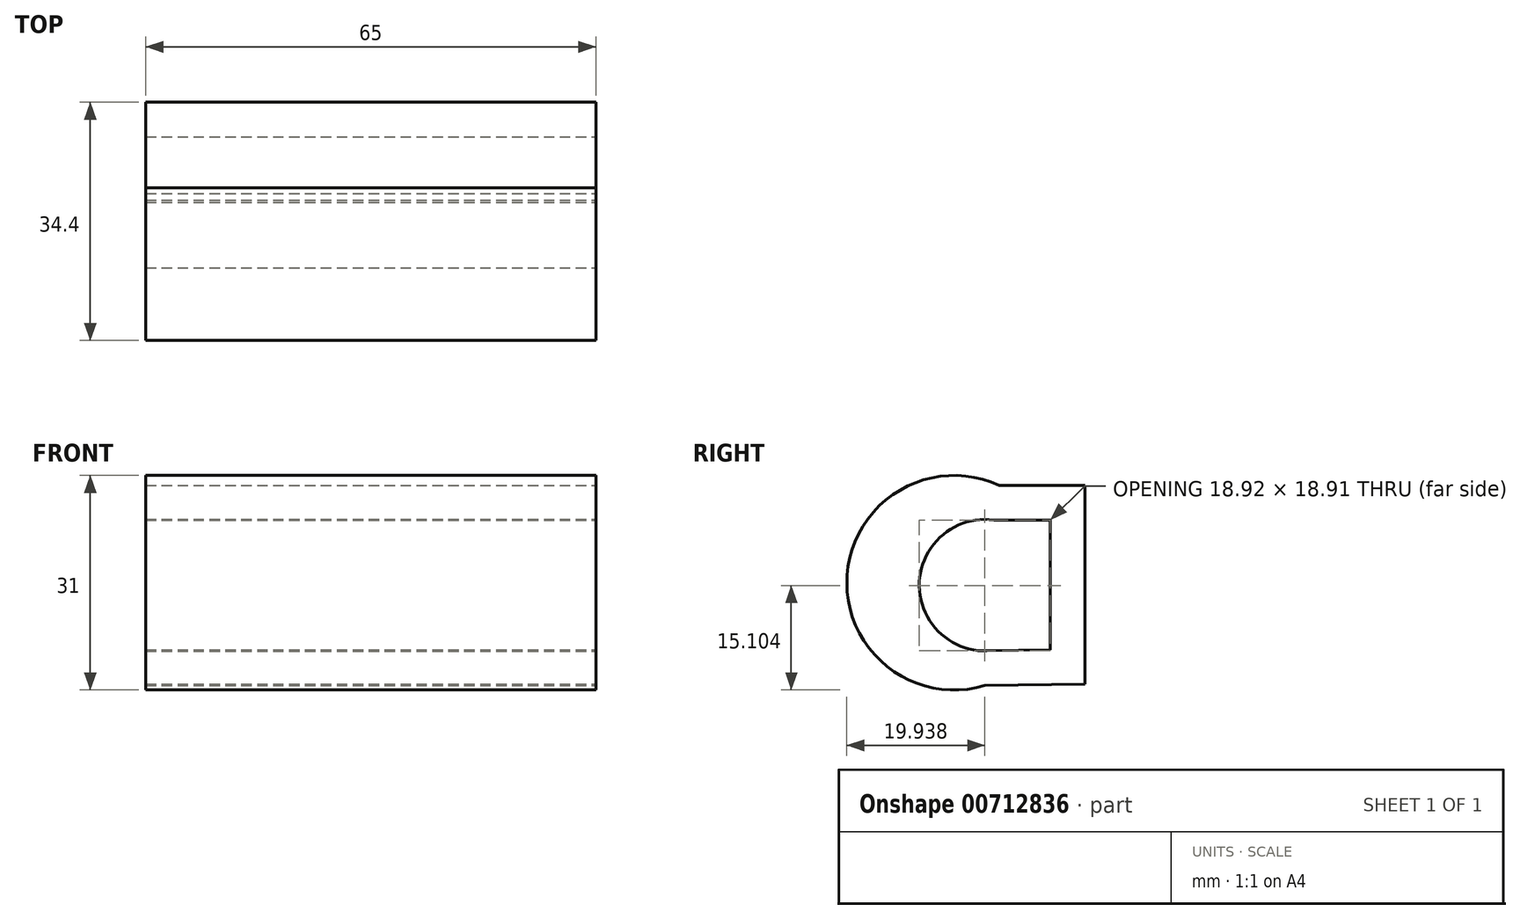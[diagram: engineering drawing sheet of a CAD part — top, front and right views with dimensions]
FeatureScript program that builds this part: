
annotation { "Feature Type Name" : "Feature", "Feature Type Description" : "" }
export const myFeature = defineFeature(function(context is Context, id is Id, definition is map)
    precondition{}
    {
        {
            var Q0;
            Q0=qCreatedBy(makeId("Top.planeOp"),FACE);
            var sketch = newSketch(context, id + "F0", { "sketchPlane" : qUnion([Q0])});
            skLineSegment(sketch, "E0", {"start": v(-20.2, -34) * mm, "end": v(44.8, -34) * mm});
            skPoint(sketch, "E1.visualSharp", {"position": v(-30.2, -34) * mm});
            skPoint(sketch, "E2.start.orphan", {"position": v(-30.2, 0) * mm});
            skSolve(sketch);
        }
        {
            var Q0;
            Q0=qCreatedBy(makeId("Right.planeOp"),FACE);
            var sketch = newSketch(context, id + "F1", { "sketchPlane" : qUnion([Q0])});
            skArc(sketch, "E3", {"start": v(-52.15, 41.38) * mm, "mid": v(-62.9, 32.45) * mm, "end": v(-53.12, 22.47) * mm});
            skLineSegment(sketch, "E4", {"start": v(-53.4, 22.46) * mm, "end": v(-43.97, 22.6) * mm});
            skLineSegment(sketch, "E5", {"start": v(-54.66, 41.38) * mm, "end": v(-43.97, 41.38) * mm});
            skLineSegment(sketch, "E6", {"start": v(-43.97, 41.38) * mm, "end": v(-43.97, 22.6) * mm});
            skArc(sketch, "E7.trimOffspring", {"start": v(-51.35, 46.38) * mm, "mid": v(-73.33, 33.44) * mm, "end": v(-53.45, 17.46) * mm});
            skLineSegment(sketch, "E8.0", {"start": v(-53.77, 17.46) * mm, "end": v(-38.97, 17.68) * mm});
            skLineSegment(sketch, "E8.1", {"start": v(-38.97, 46.38) * mm, "end": v(-38.97, 17.68) * mm});
            skLineSegment(sketch, "E8.2", {"start": v(-54.12, 46.38) * mm, "end": v(-38.97, 46.38) * mm});
            skSolve(sketch);
        }
        {
            var Q0;
            {var subQ6=sQuery(id+"F1.wireOp",EDGE,"E6");Q0=makeQuery(id+"F1.imprint","IMPRINT",FACE,{"disambiguationData":[TD([[makeQuery(id+"F1.imprint","IMPRINT",EDGE,{"derivedFrom":subQ6}),1.0]])]});}
            var Q1;
            Q1=sQuery(id+"F0.wireOp",EDGE,"E0");
            var Q2;
            Q2=sQuery(id+"F0.wireOp",EDGE,"E1.filletArc");
            var Q3;
            Q3=sQuery(id+"F0.wireOp",EDGE,"E2");
            sweep(context, id + "F2", {"profiles" : qUnion([Q0]), "path" : qUnion([Q1, Q2, Q3])});
        }
    });
